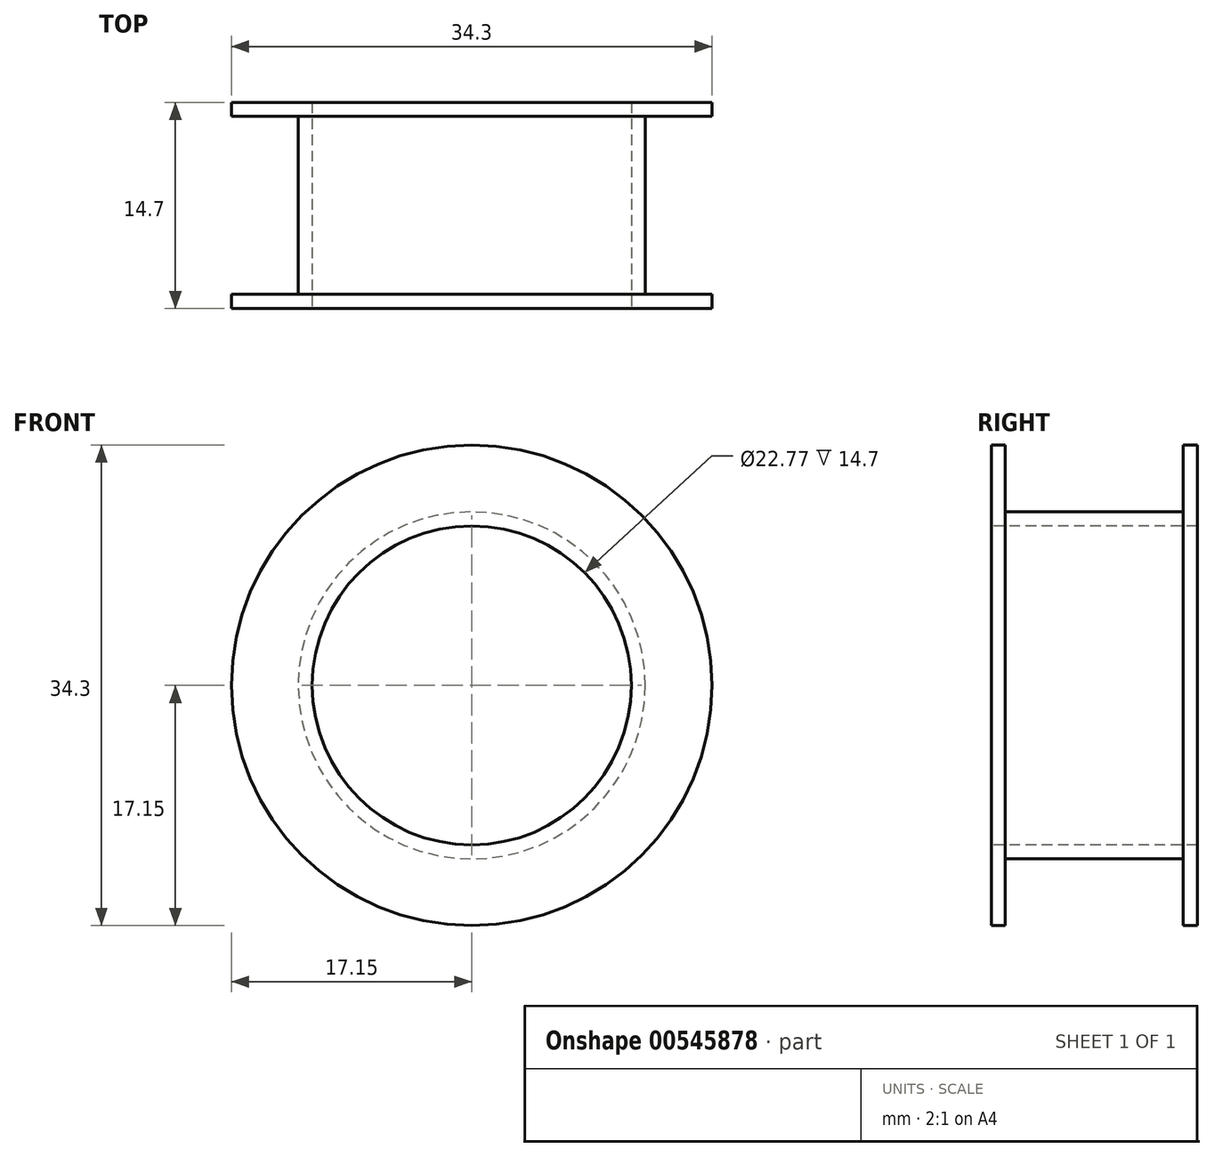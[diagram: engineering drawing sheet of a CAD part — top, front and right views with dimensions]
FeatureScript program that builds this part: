
annotation { "Feature Type Name" : "Feature", "Feature Type Description" : "" }
export const myFeature = defineFeature(function(context is Context, id is Id, definition is map)
    precondition{}
    {
        {
            var Q0;
            Q0=qCreatedBy(makeId("Top.planeOp"),FACE);
            var sketch = newSketch(context, id + "F0", { "sketchPlane" : qUnion([Q0])});
            skLineSegment(sketch, "E0", {"start": v(0, 0) * mm, "end": v(17.14, 0) * mm, "construction": true});
            skCircle(sketch, "E1", {"center": v(0, 0) * mm, "radius": 8.9 * mm, "construction": true});
            skLineSegment(sketch, "E2", {"start": v(17.15, 6.35) * mm, "end": v(12.38, 6.35) * mm});
            skLineSegment(sketch, "E3", {"start": v(17.15, -6.35) * mm, "end": v(12.38, -6.35) * mm});
            skLineSegment(sketch, "E4", {"start": v(0, -15.82) * mm, "end": v(0, 21.52) * mm, "construction": true});
            skLineSegment(sketch, "E5.0", {"start": v(17.15, -7.35) * mm, "end": v(11.38, -7.35) * mm});
            skLineSegment(sketch, "E5.2", {"start": v(17.15, 7.35) * mm, "end": v(11.38, 7.35) * mm});
            skLineSegment(sketch, "E6", {"start": v(17.15, 7.35) * mm, "end": v(17.15, 6.35) * mm});
            skLineSegment(sketch, "E7", {"start": v(17.14, -6.35) * mm, "end": v(17.15, -7.35) * mm});
            skLineSegment(sketch, "E8", {"start": v(11.38, 7.35) * mm, "end": v(11.38, -7.35) * mm});
            skLineSegment(sketch, "E9", {"start": v(12.38, 6.35) * mm, "end": v(12.38, -6.35) * mm});
            skSolve(sketch);
        }
        {
            var Q0;
            Q0 = qSketchRegion(id + "F0", true);
            var Q1;
            Q1=sQuery(id+"F0.wireOp",EDGE,"E4");
            revolve(context, id + "F1", {"entities" : qUnion([Q0]), "axis" : qUnion([Q1]), "revolveType" : RevolveType.FULL});
        }
    });
